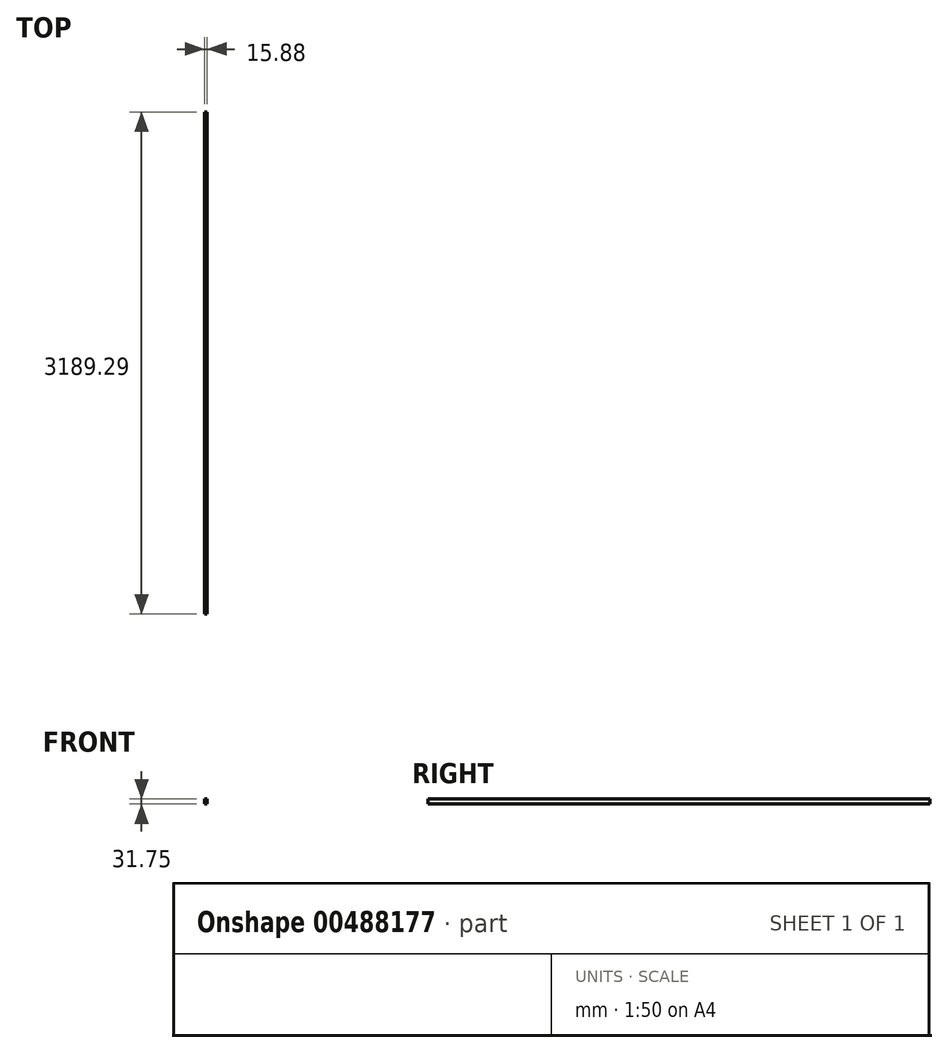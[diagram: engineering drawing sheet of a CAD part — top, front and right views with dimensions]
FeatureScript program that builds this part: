
annotation { "Feature Type Name" : "Feature", "Feature Type Description" : "" }
export const myFeature = defineFeature(function(context is Context, id is Id, definition is map)
    precondition{}
    {
        {
            var Q0;
            Q0=qCreatedBy(makeId("Front.planeOp"),FACE);
            var sketch = newSketch(context, id + "F0", { "sketchPlane" : qUnion([Q0])});
            skLineSegment(sketch, "E0", {"start": v(0, 0) * mm, "end": v(0, 31.75) * mm});
            skLineSegment(sketch, "E1", {"start": v(0, 31.75) * mm, "end": v(15.88, 31.75) * mm});
            skLineSegment(sketch, "E2", {"start": v(15.88, 31.75) * mm, "end": v(15.88, 0) * mm});
            skLineSegment(sketch, "E3", {"start": v(15.88, 0) * mm, "end": v(0, 0) * mm});
            skSolve(sketch);
        }
        {
            var Q0;
            Q0=makeQuery(id+"F0.imprint","IMPRINT",FACE,{"disambiguationData":[TD([[makeQuery(id+"F0.imprint","IMPRINT",EDGE,{"derivedFrom":sQuery(id+"F0.wireOp",EDGE,"E0")}),-1.0]])]});
            extrude(context, id + "F1", {"entities" : qUnion([Q0]), "oppositeDirection" : true, "depth" : 3189.29 * mm, "offsetDistance" : 25.4 * mm});
        }
    });
